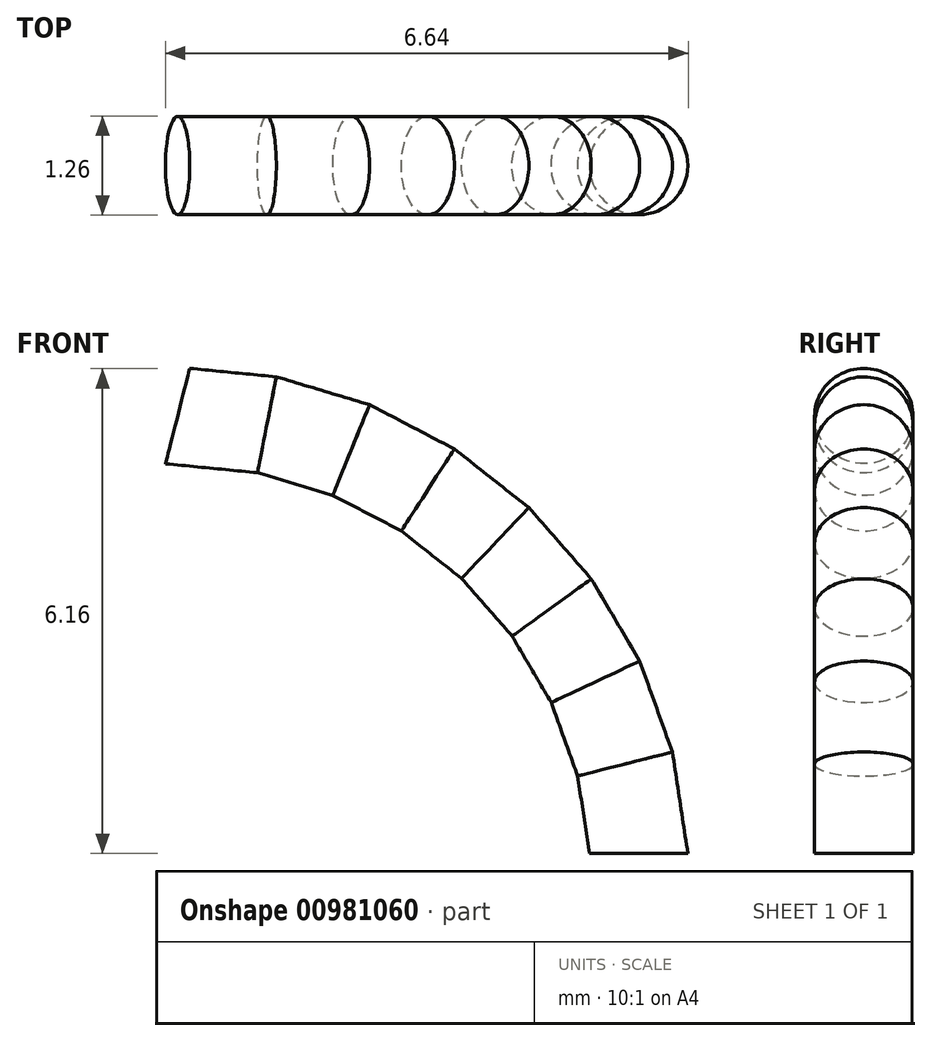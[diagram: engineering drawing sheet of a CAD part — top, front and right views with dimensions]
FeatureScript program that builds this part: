
annotation { "Feature Type Name" : "Feature", "Feature Type Description" : "" }
export const myFeature = defineFeature(function(context is Context, id is Id, definition is map)
    precondition{}
    {
        {
            var Q0;
            Q0=qCreatedBy(makeId("Front.planeOp"),FACE);
            var sketch = newSketch(context, id + "F0", { "sketchPlane" : qUnion([Q0])});
            skLineSegment(sketch, "E0", {"start": v(0, 0.01) * mm, "end": v(0, 0.01) * mm});
            skLineSegment(sketch, "E1", {"start": v(0, 0.01) * mm, "end": v(-0.18, 1.14) * mm});
            skLineSegment(sketch, "E2", {"start": v(-0.18, 1.14) * mm, "end": v(-0.55, 2.18) * mm});
            skLineSegment(sketch, "E3", {"start": v(-0.55, 2.18) * mm, "end": v(-1.1, 3.12) * mm});
            skLineSegment(sketch, "E4", {"start": v(-1.1, 3.12) * mm, "end": v(-1.82, 3.94) * mm});
            skLineSegment(sketch, "E5", {"start": v(-1.82, 3.94) * mm, "end": v(-2.68, 4.62) * mm});
            skLineSegment(sketch, "E6", {"start": v(-2.68, 4.62) * mm, "end": v(-3.65, 5.12) * mm});
            skLineSegment(sketch, "E7", {"start": v(-3.65, 5.12) * mm, "end": v(-4.72, 5.44) * mm});
            skLineSegment(sketch, "E8", {"start": v(-4.72, 5.44) * mm, "end": v(-5.87, 5.56) * mm});
            skSolve(sketch);
        }
        {
            var Q0;
            Q0=qCreatedBy(makeId("Top.planeOp"),FACE);
            var sketch = newSketch(context, id + "F1", { "sketchPlane" : qUnion([Q0])});
            skCircle(sketch, "E9", {"center": v(0, 0) * mm, "radius": 0.63 * mm});
            skSolve(sketch);
        }
        {
            var Q0;
            Q0=makeQuery(id+"F1.imprint","IMPRINT",FACE,{"disambiguationData":[TD([[makeQuery(id+"F1.imprint","IMPRINT",EDGE,{"derivedFrom":sQuery(id+"F1.wireOp",EDGE,"E9")}),1.0]])]});
            var Q1;
            Q1=sQuery(id+"F0.wireOp",EDGE,"E1");
            var Q2;
            Q2=sQuery(id+"F0.wireOp",EDGE,"E2");
            var Q3;
            Q3=sQuery(id+"F0.wireOp",EDGE,"E3");
            var Q4;
            Q4=sQuery(id+"F0.wireOp",EDGE,"E4");
            var Q5;
            Q5=sQuery(id+"F0.wireOp",EDGE,"E5");
            var Q6;
            Q6=sQuery(id+"F0.wireOp",EDGE,"E6");
            var Q7;
            Q7=sQuery(id+"F0.wireOp",EDGE,"E7");
            var Q8;
            Q8=sQuery(id+"F0.wireOp",EDGE,"E8");
            sweep(context, id + "F2", {"profiles" : qUnion([Q0]), "path" : qUnion([Q1, Q2, Q3, Q4, Q5, Q6, Q7, Q8])});
        }
    });
